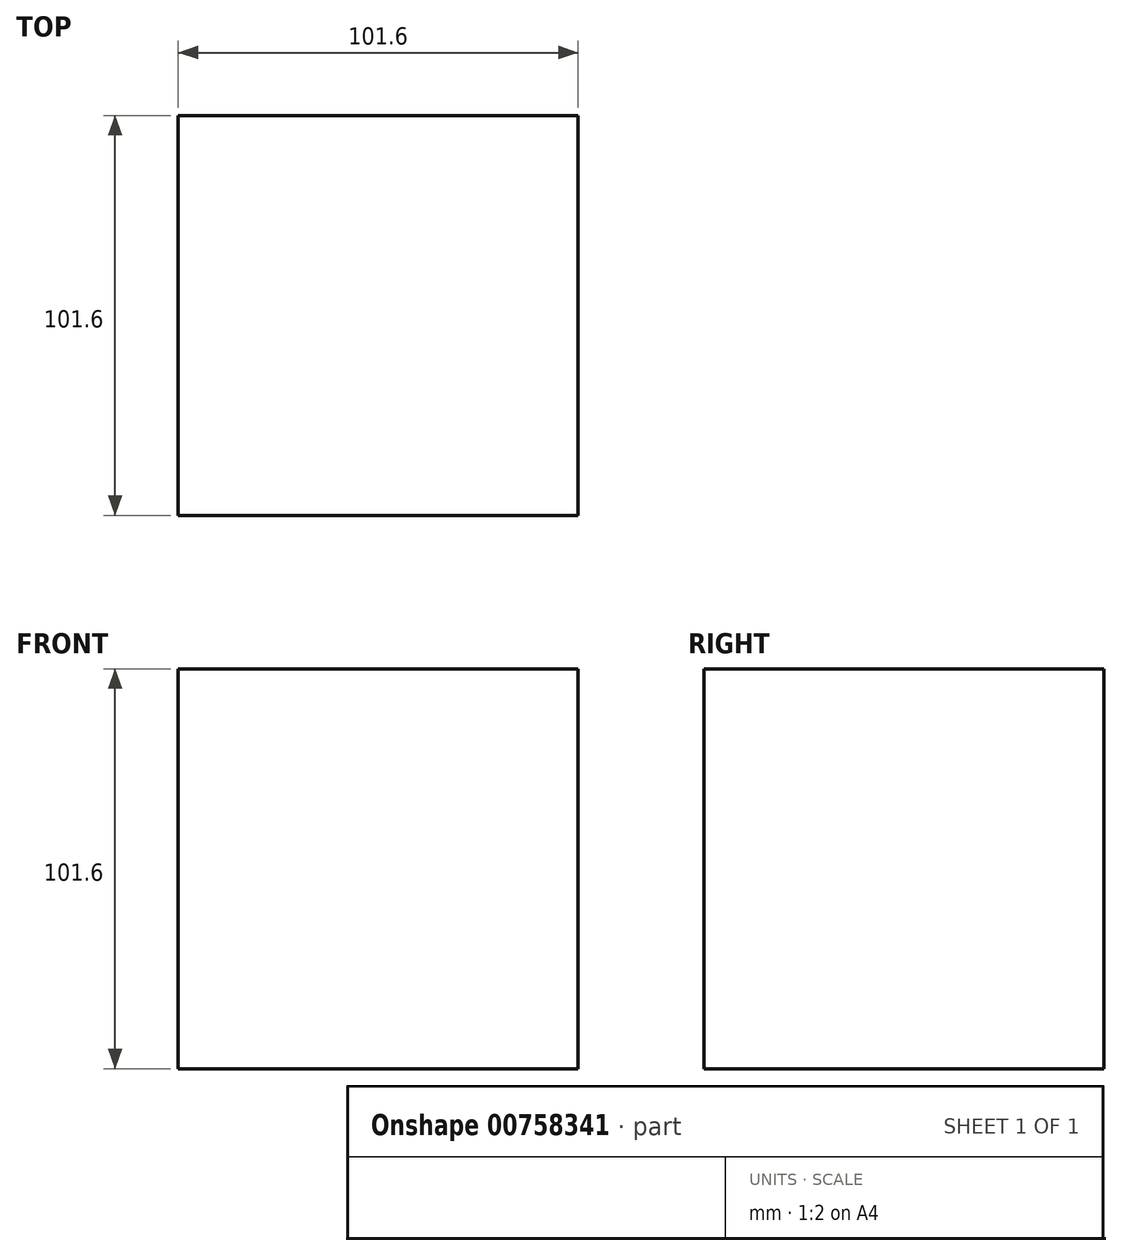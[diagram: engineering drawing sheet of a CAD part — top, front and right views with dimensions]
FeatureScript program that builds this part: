
annotation { "Feature Type Name" : "Feature", "Feature Type Description" : "" }
export const myFeature = defineFeature(function(context is Context, id is Id, definition is map)
    precondition{}
    {
        {
            var Q0;
            Q0=qCreatedBy(makeId("Top.planeOp"),FACE);
            var sketch = newSketch(context, id + "F0", { "sketchPlane" : qUnion([Q0])});
            skLineSegment(sketch, "E0.bottom", {"start": v(50.8, -50.8) * mm, "end": v(-50.8, -50.8) * mm});
            skLineSegment(sketch, "E0.top", {"start": v(50.8, 50.8) * mm, "end": v(-50.8, 50.8) * mm});
            skLineSegment(sketch, "E0.left", {"start": v(50.8, -50.8) * mm, "end": v(50.8, 50.8) * mm});
            skLineSegment(sketch, "E0.right", {"start": v(-50.8, -50.8) * mm, "end": v(-50.8, 50.8) * mm});
            skPoint(sketch, "E0.middle", {"position": v(0, 0) * mm});
            skSolve(sketch);
        }
        {
            var Q0;
            Q0=makeQuery(id+"F0.imprint","IMPRINT",FACE,{"disambiguationData":[TD([[makeQuery(id+"F0.imprint","IMPRINT",EDGE,{"derivedFrom":sQuery(id+"F0.wireOp",EDGE,"E0.bottom")}),-1.0]])]});
            extrude(context, id + "F1", {"entities" : qUnion([Q0]), "depth" : 101.6 * mm, "offsetDistance" : 25.4 * mm});
        }
    });
